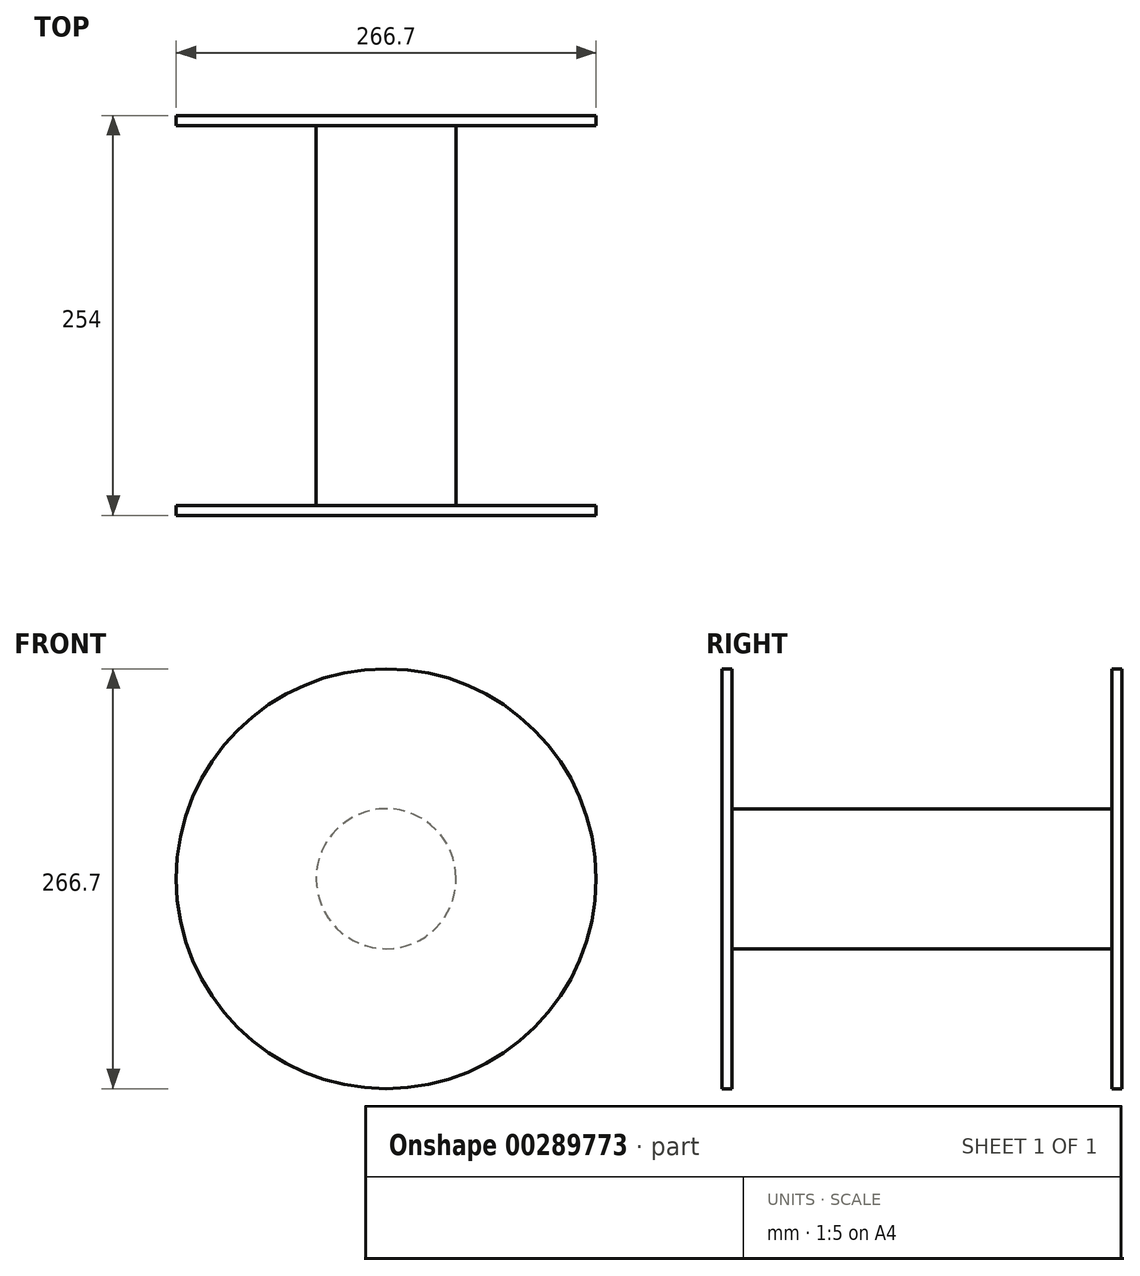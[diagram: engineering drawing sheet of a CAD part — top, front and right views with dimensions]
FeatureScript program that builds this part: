
annotation { "Feature Type Name" : "Feature", "Feature Type Description" : "" }
export const myFeature = defineFeature(function(context is Context, id is Id, definition is map)
    precondition{}
    {
        {
            var Q0;
            Q0=qCreatedBy(makeId("Front.planeOp"),FACE);
            var sketch = newSketch(context, id + "F0", { "sketchPlane" : qUnion([Q0])});
            skCircle(sketch, "E0", {"center": v(0, 0) * mm, "radius": 133.35 * mm});
            skSolve(sketch);
        }
        {
            var Q0;
            Q0=makeQuery(id+"F0.imprint","IMPRINT",FACE,{"disambiguationData":[TD([[makeQuery(id+"F0.imprint","IMPRINT",EDGE,{"derivedFrom":sQuery(id+"F0.wireOp",EDGE,"E0")}),1.0]])]});
            extrude(context, id + "F1", {"entities" : qUnion([Q0]), "oppositeDirection" : true, "depth" : 6.35 * mm});
        }
        {
            var Q0;
            Q0=makeQuery(id+"F1.opExtrude","CAP_FACE",FACE,{"disambiguationData":[OSD([sQuery(id+"F0.wireOp",EDGE,"E0")])],"isStart":false});
            var sketch = newSketch(context, id + "F2", { "sketchPlane" : qUnion([Q0])});
            skCircle(sketch, "E1", {"center": v(0, 0) * mm, "radius": 44.45 * mm});
            skSolve(sketch);
        }
        {
            var Q0;
            Q0=makeQuery(id+"F2.imprint","IMPRINT",FACE,{"disambiguationData":[TD([[makeQuery(id+"F2.imprint","IMPRINT",EDGE,{"derivedFrom":sQuery(id+"F2.wireOp",EDGE,"E1")}),1.0]])]});
            extrude(context, id + "F3", {"entities" : qUnion([Q0]), "operationType" : NewBodyOperationType.ADD, "depth" : 241.3 * mm});
        }
        {
            var Q0;
            Q0=makeQuery(id+"F3.opExtrude","CAP_FACE",FACE,{"disambiguationData":[OSD([sQuery(id+"F2.wireOp",EDGE,"E1")])],"isStart":false});
            var sketch = newSketch(context, id + "F4", { "sketchPlane" : qUnion([Q0])});
            skCircle(sketch, "E2", {"center": v(0, 0) * mm, "radius": 133.35 * mm});
            skSolve(sketch);
        }
        {
            var Q0;
            Q0=makeQuery(id+"F4.imprint","IMPRINT",FACE,{"disambiguationData":[TD([[makeQuery(id+"F4.imprint","IMPRINT",EDGE,{"derivedFrom":sQuery(id+"F4.wireOp",EDGE,"E2")}),1.0]])]});
            var Q1;
            Q1=makeQuery(id+"F4.imprint","IMPRINT",FACE,{"disambiguationData":[TD([[makeQuery(id+"F4.imprint","IMPRINT",EDGE,{"derivedFrom":makeQuery(id+"F3.opExtrude","CAP_EDGE",EDGE,{"disambiguationData":[OSD([sQuery(id+"F2.wireOp",EDGE,"E1")])],"isStart":false})}),1.0]])]});
            extrude(context, id + "F5", {"entities" : qUnion([Q0, Q1]), "operationType" : NewBodyOperationType.ADD, "depth" : 6.35 * mm});
        }
    });
